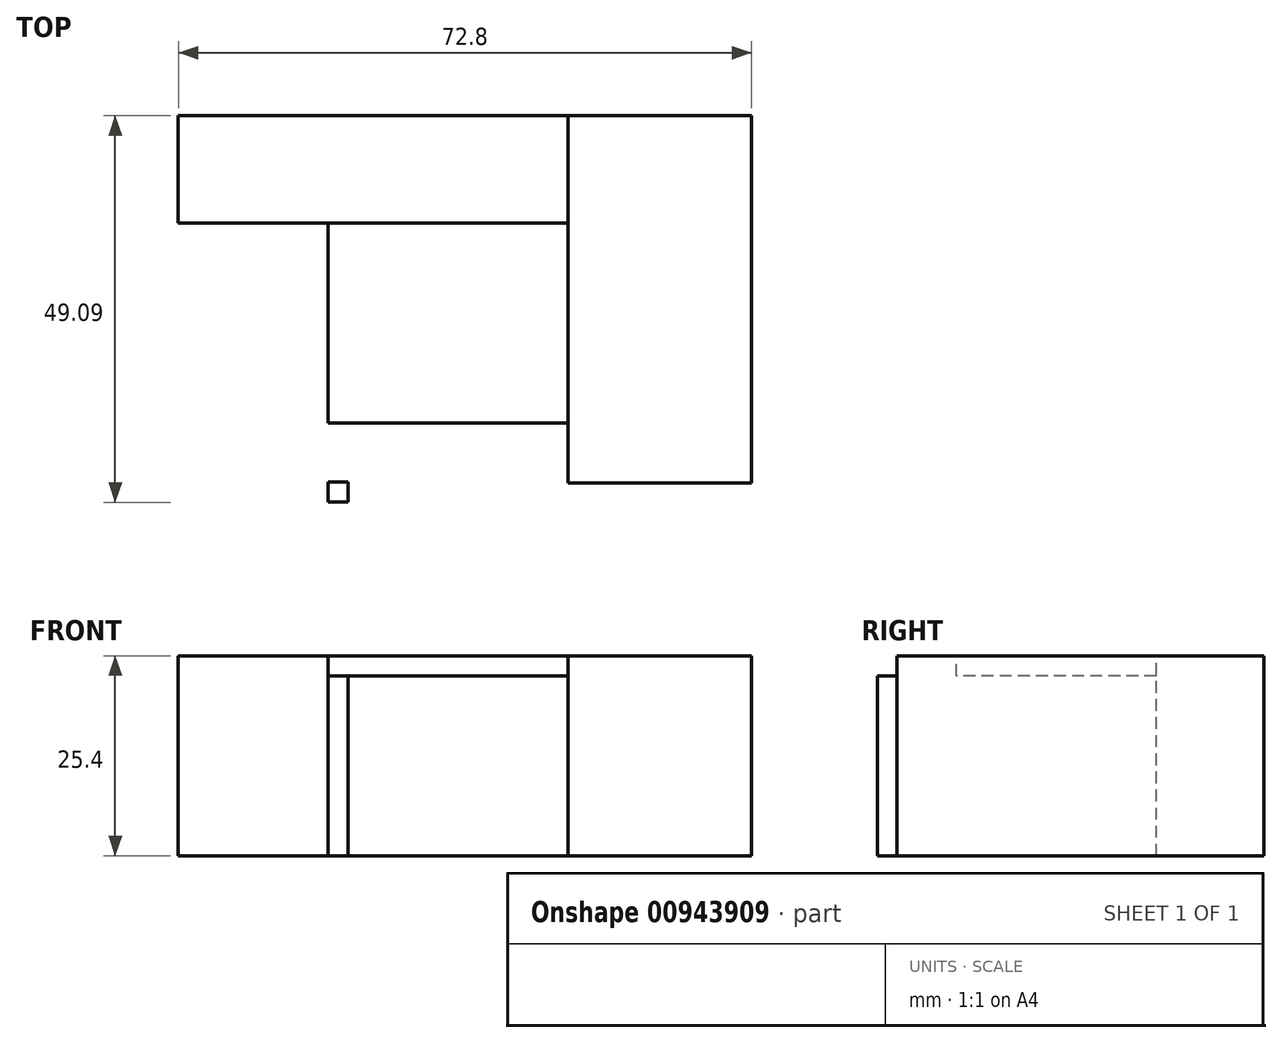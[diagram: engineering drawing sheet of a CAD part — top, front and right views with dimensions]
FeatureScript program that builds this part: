
annotation { "Feature Type Name" : "Feature", "Feature Type Description" : "" }
export const myFeature = defineFeature(function(context is Context, id is Id, definition is map)
    precondition{}
    {
        {
            var Q0;
            Q0=qCreatedBy(makeId("Top.planeOp"),FACE);
            var sketch = newSketch(context, id + "F0", { "sketchPlane" : qUnion([Q0])});
            skLineSegment(sketch, "E0.bottom", {"start": v(15.83, 10.71) * mm, "end": v(39.15, 10.71) * mm});
            skLineSegment(sketch, "E0.top", {"start": v(15.83, -35.93) * mm, "end": v(39.15, -35.93) * mm});
            skLineSegment(sketch, "E0.left", {"start": v(15.83, 10.71) * mm, "end": v(15.83, -35.93) * mm});
            skLineSegment(sketch, "E0.right", {"start": v(39.15, 10.71) * mm, "end": v(39.15, -35.93) * mm});
            skSolve(sketch);
        }
        {
            var Q0;
            Q0=makeQuery(id+"F0.imprint","IMPRINT",FACE,{"disambiguationData":[TD([[makeQuery(id+"F0.imprint","IMPRINT",EDGE,{"derivedFrom":sQuery(id+"F0.wireOp",EDGE,"E0.bottom")}),-1.0]])]});
            extrude(context, id + "F1", {"entities" : qUnion([Q0]), "depth" : 25.4 * mm, "offsetDistance" : 25.4 * mm});
        }
        {
            var Q0;
            Q0=makeQuery(id+"F1.opExtrude","CAP_FACE",FACE,{"disambiguationData":[OSD([sQuery(id+"F0.wireOp",EDGE,"E0.bottom"),sQuery(id+"F0.wireOp",EDGE,"E0.top"),sQuery(id+"F0.wireOp",EDGE,"E0.left"),sQuery(id+"F0.wireOp",EDGE,"E0.right")])],"isStart":false});
            var sketch = newSketch(context, id + "F2", { "sketchPlane" : qUnion([Q0])});
            skLineSegment(sketch, "E1.bottom", {"start": v(15.83, 10.71) * mm, "end": v(-33.65, 10.71) * mm});
            skLineSegment(sketch, "E1.top", {"start": v(15.83, -2.94) * mm, "end": v(-33.65, -2.94) * mm});
            skLineSegment(sketch, "E1.left", {"start": v(15.83, 10.71) * mm, "end": v(15.83, -2.94) * mm});
            skLineSegment(sketch, "E1.right", {"start": v(-33.65, 10.71) * mm, "end": v(-33.65, -2.94) * mm});
            skSolve(sketch);
        }
        {
            var Q0;
            Q0=makeQuery(id+"F2.imprint","IMPRINT",FACE,{"disambiguationData":[TD([[makeQuery(id+"F2.imprint","IMPRINT",EDGE,{"derivedFrom":sQuery(id+"F2.wireOp",EDGE,"E1.bottom")}),1.0]])]});
            extrude(context, id + "F3", {"entities" : qUnion([Q0]), "oppositeDirection" : true, "depth" : 25.4 * mm, "offsetDistance" : 25.4 * mm});
        }
        {
            var Q0;
            Q0=makeQuery(id+"F3.opExtrude","CAP_FACE",FACE,{"disambiguationData":[OSD([sQuery(id+"F2.wireOp",EDGE,"E1.bottom"),sQuery(id+"F2.wireOp",EDGE,"E1.top"),sQuery(id+"F2.wireOp",EDGE,"E1.left"),sQuery(id+"F2.wireOp",EDGE,"E1.right")])],"isStart":true});
            var sketch = newSketch(context, id + "F4", { "sketchPlane" : qUnion([Q0])});
            skLineSegment(sketch, "E2.bottom", {"start": v(15.83, -2.94) * mm, "end": v(-14.65, -2.94) * mm});
            skLineSegment(sketch, "E2.top", {"start": v(15.83, -28.34) * mm, "end": v(-14.65, -28.34) * mm});
            skLineSegment(sketch, "E2.left", {"start": v(15.83, -2.94) * mm, "end": v(15.83, -28.34) * mm});
            skLineSegment(sketch, "E2.right", {"start": v(-14.65, -2.94) * mm, "end": v(-14.65, -28.34) * mm});
            skSolve(sketch);
        }
        {
            var Q0;
            Q0=makeQuery(id+"F4.imprint","IMPRINT",FACE,{"disambiguationData":[TD([[makeQuery(id+"F4.imprint","IMPRINT",EDGE,{"derivedFrom":sQuery(id+"F4.wireOp",EDGE,"E2.bottom")}),1.0]])]});
            extrude(context, id + "F5", {"entities" : qUnion([Q0]), "oppositeDirection" : true, "depth" : 2.54 * mm, "offsetDistance" : 25.4 * mm});
        }
        {
            var Q0;
            Q0=makeQuery(id+"F5.opExtrude","CAP_FACE",FACE,{"disambiguationData":[OSD([sQuery(id+"F4.wireOp",EDGE,"E2.bottom"),sQuery(id+"F4.wireOp",EDGE,"E2.top"),sQuery(id+"F4.wireOp",EDGE,"E2.left"),sQuery(id+"F4.wireOp",EDGE,"E2.right")])],"isStart":false});
            cPlane(context, id + "F6", {"entities" : qUnion([Q0]), "cplaneType" : CPlaneType.OFFSET, "offset" : 22.86 * mm, "width" : 152.4 * mm, "height" : 152.4 * mm});
        }
        {
            var Q0;
            Q0=qCreatedBy(id+"F6.planeOp",FACE);
            var sketch = newSketch(context, id + "F7", { "sketchPlane" : qUnion([Q0])});
            skLineSegment(sketch, "E3.bottom", {"start": v(-14.65, 38.38) * mm, "end": v(-12.1, 38.38) * mm});
            skLineSegment(sketch, "E3.top", {"start": v(-14.65, 35.84) * mm, "end": v(-12.1, 35.84) * mm});
            skLineSegment(sketch, "E3.left", {"start": v(-14.65, 38.38) * mm, "end": v(-14.65, 35.84) * mm});
            skLineSegment(sketch, "E3.right", {"start": v(-12.1, 38.38) * mm, "end": v(-12.1, 35.84) * mm});
            skSolve(sketch);
        }
        {
            var Q0;
            Q0=makeQuery(id+"F7.imprint","IMPRINT",FACE,{"disambiguationData":[TD([[makeQuery(id+"F7.imprint","IMPRINT",EDGE,{"derivedFrom":sQuery(id+"F7.wireOp",EDGE,"E3.bottom")}),-1.0]])]});
            extrude(context, id + "F8", {"entities" : qUnion([Q0]), "oppositeDirection" : true, "depth" : 22.86 * mm, "offsetDistance" : 25.4 * mm});
        }
    });
